# Revit family: MI-FLEX-DISH
name_source: partatom
category: Pipe Fittings
units: mm (PartAtom-declared; Revit-internal decimal feet)

## family parameters
Always vertical = Yes
Classification Number = 23.60.30.11.14
Cut with Voids When Loaded = No
Part Type = Union
Round Connector Dimension = Use Diameter
Shared = Yes
Work Plane-Based = No

## types (2) — shared parameters
Assembly Code = D2090800
CW Connection = Yes
Carton Quantity = 100
Default Elevation = 0.000"
Description = MIFAB® Series MI-FLEX (specify size) of flexible rubber couplings are manufactured from an elastomeric
compound that meets the requirements of ASTM C-564 and 300 Series of stainless steel clamps tightened with 5/16” Type 300
stainless steel hex head screws. MI-FLEX Series of flexible couplings are tested and certified to ASTM Standard 1173-2010
and CSA Standard B602-2010 and listed with I.A.P.M.O.
HW Connection = No
Height = 2.700"
List Price (Each Piece) = $3.50
Manufacturer = Champion Couplings
Masking Reg 1 = No
Masking Reg 2 = Yes
Material = Plastic-Champion Couplings-Flexible PVC
Model = MI-FLEX
Nominal Diameter = 0.500"
Nominal Height = 2.700"
Pipe Inlet Connection Diameter = 1.000"
Price = Prices may vary. Please consult Manufacturer Representative for most up-to-date price list.
Product Documentation Link = MIFAB® MI-FLEX-DISH-1 dishwasher connector is manufactured out of a flexible PVC compound that meets
the requirements of ASTM C-564. Two Type 300 stainless steel clamps tightened with 5/16” Type 300 stainless steel hex head
screws provide the sealing force.
Product Page URL = http://www.mifab.com
Standard Listings & Approval = CSA Approved, U.P.C. Approved
Tick Size = 0.256"
URL = http://www.mifab.com
Vent Connection = No
Warranty Information = 1 Year Warranty
Waste Connection = No
Width A = 0.640"
Width B = 0.920"

## per-type parameters (varying)
| type | Pipe Outlet Connection Diameter | Pipe Size Description |
| MI-FLEX-DISH-1 (1" x 1") | 1.000" | 1” x 1” |
| MI-FLEX-DISH-1 (1" x .75") | 0.750" | 1” x 0.75" |

## geometry (parser evidence)
native form markers: Sweep x1
no freeform markers — native parametric forms only
